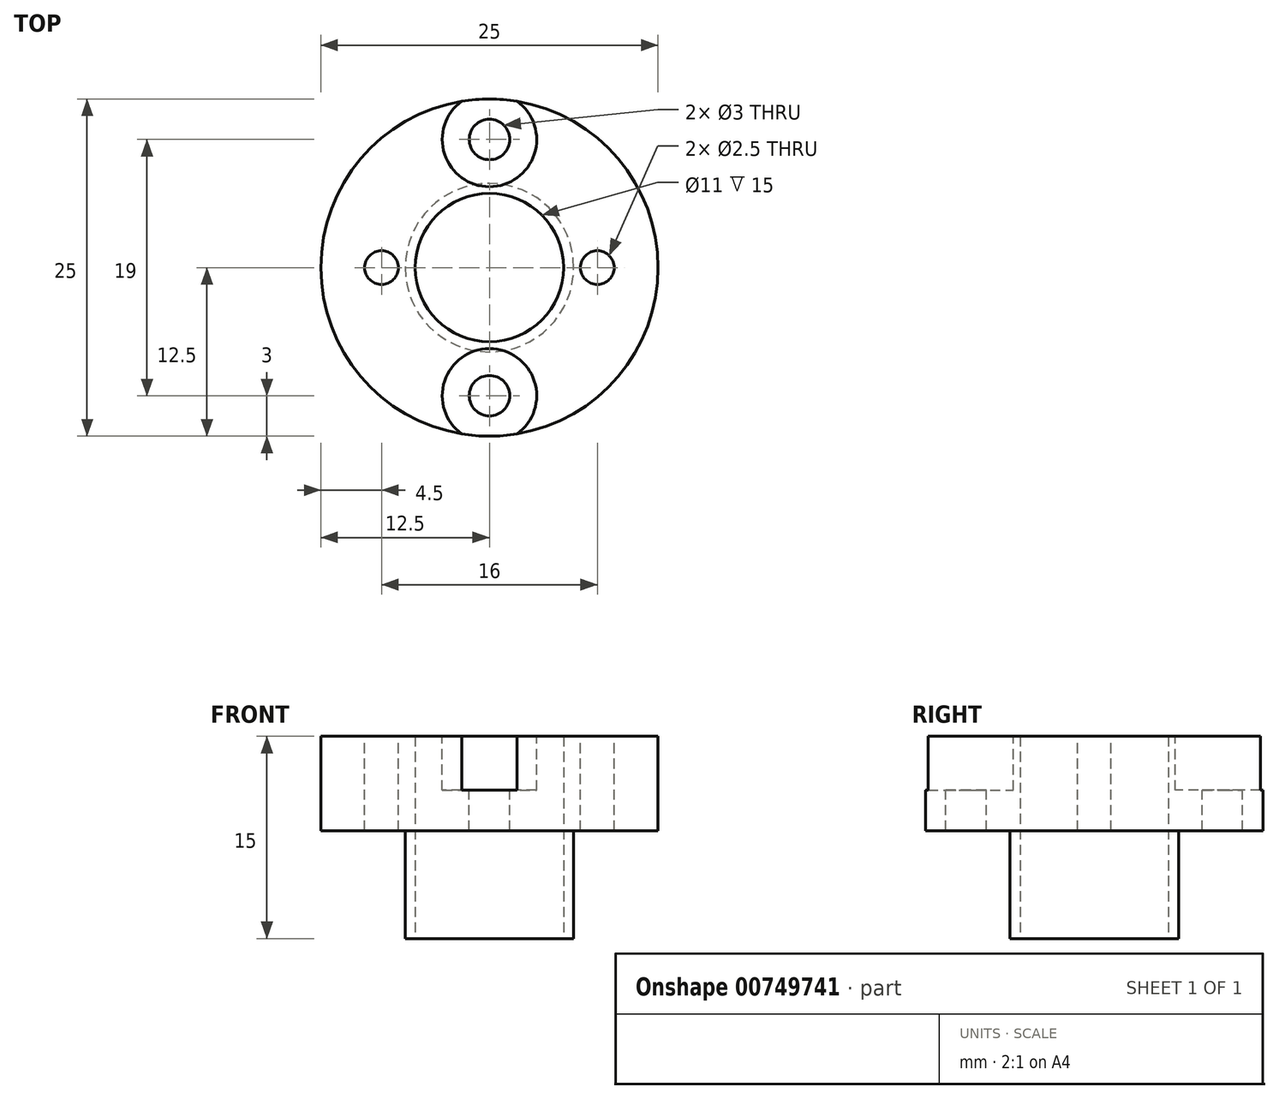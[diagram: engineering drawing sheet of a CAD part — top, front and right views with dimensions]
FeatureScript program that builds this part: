
annotation { "Feature Type Name" : "Feature", "Feature Type Description" : "" }
export const myFeature = defineFeature(function(context is Context, id is Id, definition is map)
    precondition{}
    {
        {
            var Q0;
            Q0=qCreatedBy(makeId("Top.planeOp"),FACE);
            var sketch = newSketch(context, id + "F0", { "sketchPlane" : qUnion([Q0])});
            skCircle(sketch, "E0", {"center": v(0, 0) * mm, "radius": 12.5 * mm});
            skSolve(sketch);
        }
        {
            var Q0;
            Q0 = qSketchRegion(id + "F0", true);
            extrude(context, id + "F1", {"entities" : qUnion([Q0]), "depth" : 7 * mm, "offsetDistance" : 25 * mm});
        }
        {
            var Q0;
            Q0=makeQuery(id+"F1.opExtrude","CAP_FACE",FACE,{"disambiguationData":[OSD([sQuery(id+"F0.wireOp",EDGE,"E0")])],"isStart":false});
            var sketch = newSketch(context, id + "F2", { "sketchPlane" : qUnion([Q0])});
            skCircle(sketch, "E1", {"center": v(0, 9.5) * mm, "radius": 1.5 * mm});
            skCircle(sketch, "E2", {"center": v(0, -9.5) * mm, "radius": 1.5 * mm});
            skLineSegment(sketch, "E3", {"start": v(-12.5, 0) * mm, "end": v(12.5, 0) * mm});
            skLineSegment(sketch, "E4", {"start": v(0, 9.5) * mm, "end": v(0, 0) * mm, "construction": true});
            skLineSegment(sketch, "E5", {"start": v(0, 0) * mm, "end": v(0, -9.5) * mm, "construction": true});
            skSolve(sketch);
        }
        {
            var Q0;
            Q0 = qSketchRegion(id + "F2", true);
            extrude(context, id + "F3", {"entities" : qUnion([Q0]), "operationType" : NewBodyOperationType.REMOVE, "endBound" : BoundingType.THROUGH_ALL, "oppositeDirection" : true, "depth" : 25 * mm, "offsetDistance" : 25 * mm});
        }
        {
            var Q0;
            Q0=makeQuery(id+"F1.opExtrude","CAP_FACE",FACE,{"disambiguationData":[OSD([sQuery(id+"F0.wireOp",EDGE,"E0")])],"isStart":false});
            var sketch = newSketch(context, id + "F4", { "sketchPlane" : qUnion([Q0])});
            skCircle(sketch, "E6", {"center": v(0, 9.5) * mm, "radius": 3.5 * mm});
            skCircle(sketch, "E7", {"center": v(0, -9.5) * mm, "radius": 3.5 * mm});
            skSolve(sketch);
        }
        {
            var Q0;
            Q0 = qSketchRegion(id + "F4", true);
            var Q1;
            Q1=makeQuery(id+"F1.opExtrude","CAP_FACE",FACE,{"disambiguationData":[OSD([sQuery(id+"F0.wireOp",EDGE,"E0")])],"isStart":true});
            extrude(context, id + "F5", {"entities" : qUnion([Q0]), "operationType" : NewBodyOperationType.REMOVE, "endBound" : BoundingType.UP_TO_SURFACE, "oppositeDirection" : true, "depth" : 25 * mm, "endBoundEntityFace" : qUnion([Q1]), "hasOffset" : true, "offsetDistance" : 3 * mm});
        }
        {
            var Q0;
            Q0=makeQuery(id+"F1.opExtrude","CAP_FACE",FACE,{"disambiguationData":[OSD([sQuery(id+"F0.wireOp",EDGE,"E0")])],"isStart":true});
            var sketch = newSketch(context, id + "F6", { "sketchPlane" : qUnion([Q0])});
            skCircle(sketch, "E8", {"center": v(0, 0) * mm, "radius": 5 * mm});
            skCircle(sketch, "E9", {"center": v(0, 0) * mm, "radius": 6.25 * mm});
            skSolve(sketch);
        }
        {
            var Q0;
            Q0 = qSketchRegion(id + "F6", true);
            extrude(context, id + "F7", {"entities" : qUnion([Q0]), "operationType" : NewBodyOperationType.ADD, "depth" : 8 * mm, "offsetDistance" : 25 * mm});
        }
        {
            var Q0;
            Q0=makeQuery(id+"F7.boolean.opBoolean","SPLIT",FACE,{"disambiguationData":[TD([makeQuery(id+"F7.opExtrude","SWEPT_FACE",FACE,{"disambiguationData":[OSD([sQuery(id+"F6.wireOp",EDGE,"E8")])]})])],"derivedFrom":makeQuery(id+"F1.opExtrude","CAP_FACE",FACE,{"disambiguationData":[OSD([sQuery(id+"F0.wireOp",EDGE,"E0")])],"isStart":true})});
            var sketch = newSketch(context, id + "F8", { "sketchPlane" : qUnion([Q0])});
            skCircle(sketch, "E10", {"center": v(0, 0) * mm, "radius": 5.5 * mm});
            skSolve(sketch);
        }
        {
            var Q0;
            Q0 = qSketchRegion(id + "F8", true);
            extrude(context, id + "F9", {"entities" : qUnion([Q0]), "operationType" : NewBodyOperationType.REMOVE, "endBound" : BoundingType.THROUGH_ALL, "oppositeDirection" : true, "depth" : 25 * mm, "offsetDistance" : 25 * mm, "hasSecondDirection" : true, "secondDirectionBound" : SecondDirectionBoundingType.THROUGH_ALL, "secondDirectionOppositeDirection" : false, "secondDirectionDepth" : 25 * mm});
        }
        {
            var Q0;
            Q0=makeQuery(id+"F1.opExtrude","CAP_FACE",FACE,{"disambiguationData":[OSD([sQuery(id+"F0.wireOp",EDGE,"E0")])],"isStart":false});
            var sketch = newSketch(context, id + "F10", { "sketchPlane" : qUnion([Q0])});
            skLineSegment(sketch, "E11", {"start": v(0, 0) * mm, "end": v(8, 0) * mm, "construction": true});
            skLineSegment(sketch, "E12", {"start": v(0, 0) * mm, "end": v(-8, 0) * mm, "construction": true});
            skCircle(sketch, "E13", {"center": v(8, 0) * mm, "radius": 1.25 * mm});
            skCircle(sketch, "E14", {"center": v(-8, 0) * mm, "radius": 1.25 * mm});
            skSolve(sketch);
        }
        {
            var Q0;
            Q0 = qSketchRegion(id + "F10", true);
            extrude(context, id + "F11", {"entities" : qUnion([Q0]), "operationType" : NewBodyOperationType.REMOVE, "endBound" : BoundingType.THROUGH_ALL, "oppositeDirection" : true, "depth" : 25 * mm, "offsetDistance" : 25 * mm});
        }
    });
